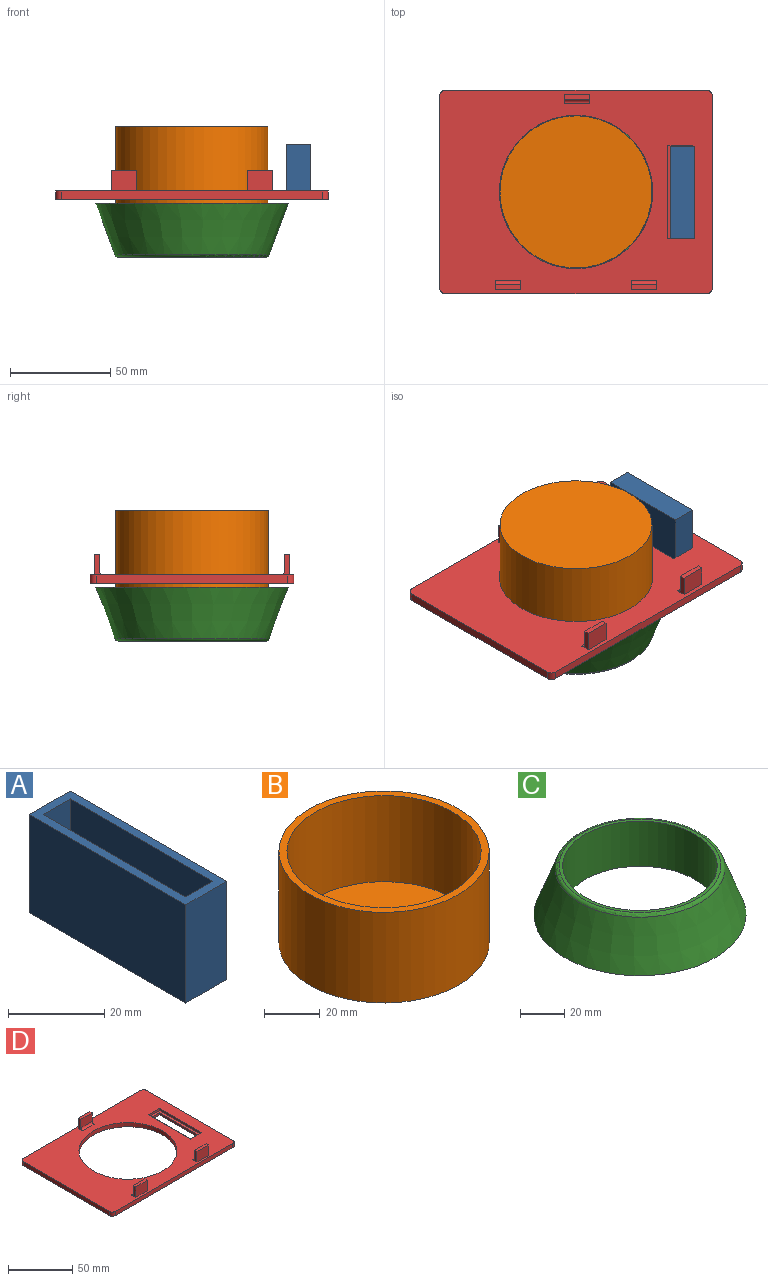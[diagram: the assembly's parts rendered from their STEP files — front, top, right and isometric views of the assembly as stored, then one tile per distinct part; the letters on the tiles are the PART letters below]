
ASSEMBLY  parts=4 mates=3
PART A: 11 faces, bbox 12x46x25 mm
  f0: plane 46x25mm, normal (-1,0,0), area 1150mm2, adj f1,f3,f4,f5
  f1: plane 25x12mm, normal (0,-1,0), area 300mm2, adj f0,f2,f4,f5
  f2: plane 46x25mm, normal (1,0,0), area 1150mm2, adj f1,f3,f4,f5
  f3: plane 25x12mm, normal (0,1,0), area 300mm2, adj f0,f2,f4,f5
  f4: plane 46x12mm, normal (0,0,1), area 216mm2, adj f0,f1,f2,f3,f6,f7,f8,f9
  f5: plane 46x12mm, normal (0,0,-1), area 552mm2, adj f0,f1,f2,f3
  f6: plane 42x23mm, normal (1,0,0), area 966mm2, adj f4,f7,f9,f10
  f7: plane 23x8mm, normal (0,1,0), area 184mm2, adj f4,f6,f8,f10
  f8: plane 42x23mm, normal (-1,0,0), area 966mm2, adj f4,f7,f9,f10
  f9: plane 23x8mm, normal (0,-1,0), area 184mm2, adj f4,f6,f8,f10
  f10: plane 42x8mm, normal (0,0,1), area 336mm2, adj f6,f7,f8,f9
PART B: 5 faces, bbox 75.8x75.8x40 mm
  f0: cylinder r=37.9mm len=75.8mm, axis (0,0,-1), area 9525.3mm2, adj f1,f2
  f1: plane 75.8x75.8mm, normal (0,0,1), area 664.2mm2, adj f0,f3
  f2: plane 75.8x75.8mm, normal (0,0,-1), area 4512.6mm2, adj f0
  f3: cylinder r=35mm len=70mm, axis (0,0,1), area 8356.6mm2, adj f1,f4
  f4: plane 70x70mm, normal (0,0,1), area 3848.5mm2, adj f3
PART C: 7 faces, bbox 96x96x27 mm
  f0: plane 76x76mm, normal (0,0,-1), area 688mm2, adj f1,f5
  f1: cylinder r=35mm len=70mm, axis (0,0,-1), area 5497.8mm2, adj f0,f2
  f2: plane 73.22x73.22mm, normal (0,0,1), area 361.7mm2, adj f1,f6
  f3: cone r=38mm half-angle=20.3deg, axis (0,0,-1), area 7444.6mm2, adj f4,f6
  f4: plane 96x96mm, normal (0,0,-1), area 2701.8mm2, adj f3,f5
  f5: cylinder r=38mm len=76mm, axis (0,0,-1), area 477.5mm2, adj f0,f4
  f6: torus R=36.61mm, axis (0,0,-1), area 575.8mm2, adj f2,f3
PART D: 38 faces, bbox 136x101.5x14 mm
  f0: plane 42x2mm, normal (-1,0,0), area 84mm2, adj f1,f3,f5,f34
  f1: plane 8x2mm, normal (0,-1,0), area 16mm2, adj f0,f2,f5,f34
  f2: plane 42x2mm, normal (1,0,0), area 84mm2, adj f1,f3,f5,f34
  f3: plane 8x2mm, normal (0,1,0), area 16mm2, adj f0,f2,f5,f34
  f4: plane 136x101.5mm, normal (0,0,1), area 8455.8mm2, adj f6,f7,f8,f9,f10,f11,f12,f13
  f5: plane 136x101.5mm, normal (0,0,-1), area 8863.9mm2, adj f0,f1,f2,f3,f6,f7,f8,f9
  f6: plane 95.5x4mm, normal (-1,0,0), area 382mm2, adj f4,f5,f26,f29
  f7: plane 130x4mm, normal (0,-1,0), area 520mm2, adj f4,f5,f26,f27
  f8: plane 95.5x4mm, normal (1,0,0), area 382mm2, adj f4,f5,f27,f28
  f9: plane 130x4mm, normal (0,1,0), area 520mm2, adj f4,f5,f28,f29
  f10: cylinder r=38.25mm len=76.5mm, axis (0,0,1), area 961.3mm2, adj f4,f5
  f11: plane 10x4.5mm, normal (-1,0,0), area 25.9mm2, adj f4,f12,f14,f15,f37
  f12: plane 12.5x10mm, normal (0,-1,0), area 125mm2, adj f4,f11,f13,f15
  f13: plane 10x4.5mm, normal (1,0,0), area 25.9mm2, adj f4,f12,f14,f15,f37
  f14: plane 12.5x8mm, normal (0,1,0), area 100mm2, adj f11,f13,f15,f37
  f15: plane 12.5x2.5mm, normal (0,0,1), area 31.3mm2, adj f11,f12,f13,f14
  f16: plane 12.5x10mm, normal (0,-1,0), area 125mm2, adj f4,f17,f19,f20
  f17: plane 10x4.5mm, normal (1,0,0), area 25.9mm2, adj f4,f16,f18,f20,f36
  f18: plane 12.5x8mm, normal (0,1,0), area 100mm2, adj f17,f19,f20,f36
  f19: plane 10x4.5mm, normal (-1,0,0), area 25.9mm2, adj f4,f16,f18,f20,f36
  f20: plane 12.5x2.5mm, normal (0,0,1), area 31.2mm2, adj f16,f17,f18,f19
  f21: plane 10x4.5mm, normal (-1,0,0), area 25.9mm2, adj f4,f22,f24,f25,f35
  f22: plane 12.5x8mm, normal (0,-1,0), area 100mm2, adj f21,f23,f25,f35
  f23: plane 10x4.5mm, normal (1,0,0), area 25.9mm2, adj f4,f22,f24,f25,f35
  f24: plane 12.5x10mm, normal (0,1,0), area 125mm2, adj f4,f21,f23,f25
  f25: plane 12.5x2.5mm, normal (0,0,1), area 31.2mm2, adj f21,f22,f23,f24
  f26: cylinder r=3mm len=4mm, axis (0,0,1), area 18.8mm2, adj f4,f5,f6,f7
  f27: cylinder r=3mm len=4mm, axis (0,0,-1), area 18.8mm2, adj f4,f5,f7,f8
  f28: cylinder r=3mm len=4mm, axis (0,0,1), area 18.8mm2, adj f4,f5,f8,f9
  f29: cylinder r=3mm len=4mm, axis (0,0,-1), area 18.8mm2, adj f4,f5,f6,f9
  f30: plane 46.4x2mm, normal (1,0,0), area 92.8mm2, adj f4,f31,f33,f34
  f31: plane 12.4x2mm, normal (0,1,0), area 24.8mm2, adj f4,f30,f32,f34
  f32: plane 46.4x2mm, normal (-1,0,0), area 92.8mm2, adj f4,f31,f33,f34
  f33: plane 12.4x2mm, normal (0,-1,0), area 24.8mm2, adj f4,f30,f32,f34
  f34: plane 46.4x12.4mm, normal (0,0,1), area 239.4mm2, adj f0,f1,f2,f3,f30,f31,f32,f33
  f35: cylinder r=2mm len=12.5mm, axis (1,0,0), area 39.3mm2, adj f4,f21,f22,f23
  f36: cylinder r=2mm len=12.5mm, axis (-1,0,0), area 39.3mm2, adj f4,f17,f18,f19
  f37: cylinder r=2mm len=12.5mm, axis (-1,0,0), area 39.3mm2, adj f4,f11,f13,f14
PLACE A rot(axis=(1,0,0),180deg) t=(255.51,36.45,29.17)mm
PLACE B rot(axis=(0,-1,0),180deg) t=(208.41,13.65,38.17)mm
PLACE C rot(axis=(0,-1,0),180deg) t=(208.41,13.65,0.17)mm
PLACE D t=(140.41,-37.1,2.17)mm
MATE slider D.f10 <-> B.f0  axis (0,0,1) through (208.41,13.65,6.17)mm
MATE pin_slot A.f4 <-> D.f34  axis (0,0,-1) through (267.51,-9.55,4.17)mm
MATE slider C.f1 <-> B.f0  axis (0,0,1) through (208.41,13.65,-1.83)mm
